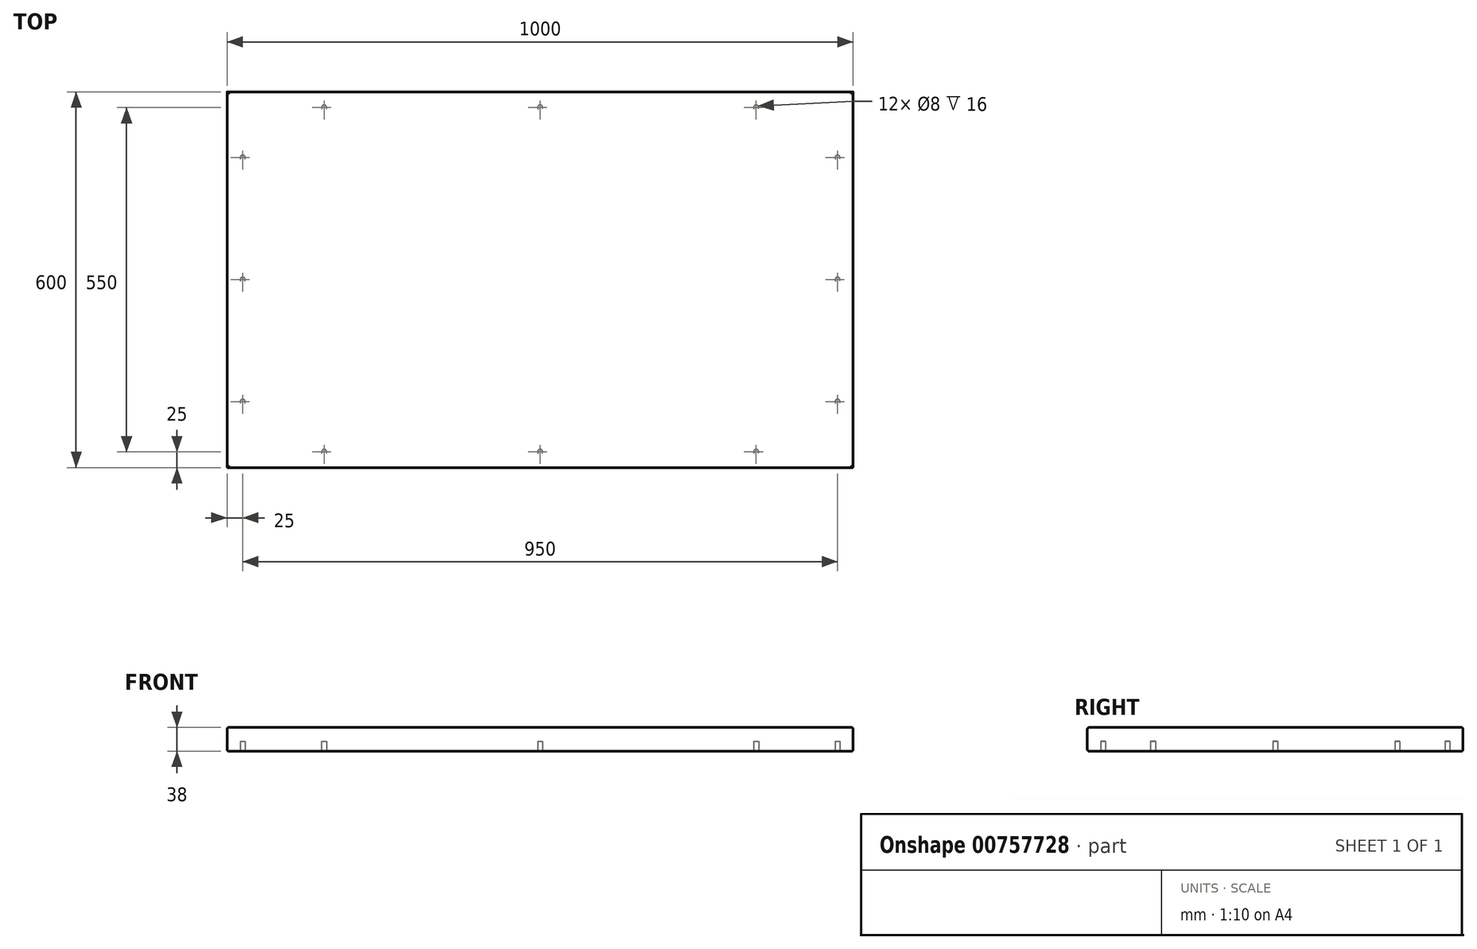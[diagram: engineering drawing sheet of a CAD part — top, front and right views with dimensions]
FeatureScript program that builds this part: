
annotation { "Feature Type Name" : "Feature", "Feature Type Description" : "" }
export const myFeature = defineFeature(function(context is Context, id is Id, definition is map)
    precondition{}
    {
        {
            var Q0;
            Q0=qCreatedBy(makeId("Top.planeOp"),FACE);
            var sketch = newSketch(context, id + "F0", { "sketchPlane" : qUnion([Q0])});
            skLineSegment(sketch, "E0.bottom", {"start": v(500, -300) * mm, "end": v(-500, -300) * mm});
            skLineSegment(sketch, "E0.top", {"start": v(500, 300) * mm, "end": v(-500, 300) * mm});
            skLineSegment(sketch, "E0.left", {"start": v(500, -300) * mm, "end": v(500, 300) * mm});
            skLineSegment(sketch, "E0.right", {"start": v(-500, -300) * mm, "end": v(-500, 300) * mm});
            skPoint(sketch, "E0.middle", {"position": v(0, 0) * mm});
            skSolve(sketch);
        }
        {
            var Q0;
            Q0=makeQuery(id+"F0.imprint","IMPRINT",FACE,{"disambiguationData":[TD([[makeQuery(id+"F0.imprint","IMPRINT",EDGE,{"derivedFrom":sQuery(id+"F0.wireOp",EDGE,"E0.bottom")}),-1.0]])]});
            extrude(context, id + "F1", {"entities" : qUnion([Q0]), "depth" : 38 * mm, "offsetDistance" : 25 * mm});
        }
        {
            var Q0;
            Q0=makeQuery(id+"F1.opExtrude","CAP_EDGE",EDGE,{"disambiguationData":[OSD([sQuery(id+"F0.wireOp",EDGE,"E0.top")])],"isStart":false});
            var Q1;
            Q1=makeQuery(id+"F1.opExtrude","CAP_EDGE",EDGE,{"disambiguationData":[OSD([sQuery(id+"F0.wireOp",EDGE,"E0.left")])],"isStart":false});
            var Q2;
            Q2=makeQuery(id+"F1.opExtrude","CAP_EDGE",EDGE,{"disambiguationData":[OSD([sQuery(id+"F0.wireOp",EDGE,"E0.bottom")])],"isStart":false});
            var Q3;
            Q3=makeQuery(id+"F1.opExtrude","CAP_EDGE",EDGE,{"disambiguationData":[OSD([sQuery(id+"F0.wireOp",EDGE,"E0.right")])],"isStart":false});
            var Q4;
            Q4=makeQuery(id+"F1.opExtrude","CAP_EDGE",EDGE,{"disambiguationData":[OSD([sQuery(id+"F0.wireOp",EDGE,"E0.left")])],"isStart":true});
            var Q5;
            Q5=makeQuery(id+"F1.opExtrude","CAP_EDGE",EDGE,{"disambiguationData":[OSD([sQuery(id+"F0.wireOp",EDGE,"E0.top")])],"isStart":true});
            var Q6;
            Q6=makeQuery(id+"F1.opExtrude","CAP_EDGE",EDGE,{"disambiguationData":[OSD([sQuery(id+"F0.wireOp",EDGE,"E0.right")])],"isStart":true});
            var Q7;
            Q7=makeQuery(id+"F1.opExtrude","CAP_EDGE",EDGE,{"disambiguationData":[OSD([sQuery(id+"F0.wireOp",EDGE,"E0.bottom")])],"isStart":true});
            fillet(context, id + "F2", {"entities" : qUnion([Q0, Q1, Q2, Q3, Q4, Q5, Q6, Q7]), "radius" : 3 * mm, "tangentPropagation" : true, "allowEdgeOverflow" : false});
        }
        {
            var Q0;
            Q0=makeQuery(id+"F1.opExtrude","CAP_FACE",FACE,{"disambiguationData":[OSD([sQuery(id+"F0.wireOp",EDGE,"E0.bottom"),sQuery(id+"F0.wireOp",EDGE,"E0.top"),sQuery(id+"F0.wireOp",EDGE,"E0.left"),sQuery(id+"F0.wireOp",EDGE,"E0.right")])],"isStart":true});
            var sketch = newSketch(context, id + "F3", { "sketchPlane" : qUnion([Q0])});
            skCircle(sketch, "E1", {"center": v(-345, 275) * mm, "radius": 4 * mm});
            skCircle(sketch, "E2", {"center": v(0, 275) * mm, "radius": 4 * mm});
            skCircle(sketch, "E3", {"center": v(345, 275) * mm, "radius": 4 * mm});
            skLineSegment(sketch, "E4", {"start": v(-497, 0) * mm, "end": v(497, 0) * mm, "construction": true});
            skLineSegment(sketch, "E5", {"start": v(0, 297) * mm, "end": v(0, -297) * mm, "construction": true});
            skCircle(sketch, "E6.MirrorC", {"center": v(345, -275) * mm, "radius": 4 * mm});
            skCircle(sketch, "E7.MirrorC", {"center": v(0, -275) * mm, "radius": 4 * mm});
            skCircle(sketch, "E8.MirrorC", {"center": v(-345, -275) * mm, "radius": 4 * mm});
            skCircle(sketch, "E9", {"center": v(-475, 0) * mm, "radius": 4 * mm});
            skCircle(sketch, "E10", {"center": v(-475, -195) * mm, "radius": 4 * mm});
            skCircle(sketch, "E11", {"center": v(-475, 195) * mm, "radius": 4 * mm});
            skCircle(sketch, "E12.MirrorC", {"center": v(475, 195) * mm, "radius": 4 * mm});
            skCircle(sketch, "E13.MirrorC", {"center": v(475, 0) * mm, "radius": 4 * mm});
            skCircle(sketch, "E14.MirrorC", {"center": v(475, -195) * mm, "radius": 4 * mm});
            skSolve(sketch);
        }
        {
            var Q0;
            Q0 = qSketchRegion(id + "F3", true);
            extrude(context, id + "F4", {"entities" : qUnion([Q0]), "operationType" : NewBodyOperationType.REMOVE, "oppositeDirection" : true, "depth" : 16 * mm, "offsetDistance" : 25 * mm});
        }
    });
